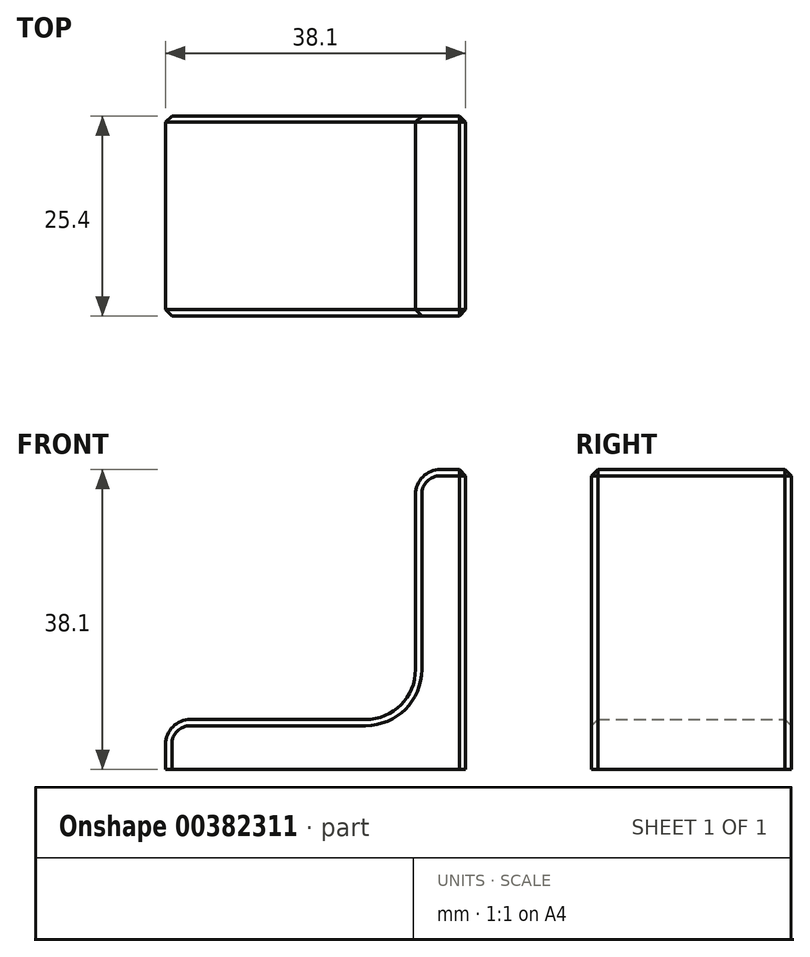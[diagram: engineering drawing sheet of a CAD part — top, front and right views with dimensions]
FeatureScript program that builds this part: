
annotation { "Feature Type Name" : "Feature", "Feature Type Description" : "" }
export const myFeature = defineFeature(function(context is Context, id is Id, definition is map)
    precondition{}
    {
        {
            var Q0;
            Q0=qCreatedBy(makeId("Front.planeOp"),FACE);
            var sketch = newSketch(context, id + "F0", { "sketchPlane" : qUnion([Q0])});
            skLineSegment(sketch, "E0", {"start": v(0, 38.1) * mm, "end": v(0, 0) * mm});
            skLineSegment(sketch, "E1", {"start": v(0, 0) * mm, "end": v(-38.1, 0) * mm});
            skLineSegment(sketch, "E2", {"start": v(-38.1, 0) * mm, "end": v(-38.1, 3.17) * mm});
            skLineSegment(sketch, "E3", {"start": v(0, 38.1) * mm, "end": v(-3.17, 38.1) * mm});
            skLineSegment(sketch, "E4", {"start": v(-6.35, 34.93) * mm, "end": v(-6.35, 12.7) * mm});
            skLineSegment(sketch, "E5", {"start": v(-34.93, 6.35) * mm, "end": v(-12.7, 6.35) * mm});
            skPoint(sketch, "E6.visualSharp", {"position": v(-6.35, 38.1) * mm});
            skArc(sketch, "E6.filletArc", {"start": v(-3.17, 38.1) * mm, "mid": v(-5.42, 37.17) * mm, "end": v(-6.35, 34.93) * mm});
            skPoint(sketch, "E7.visualSharp", {"position": v(-38.1, 6.35) * mm});
            skArc(sketch, "E7.filletArc", {"start": v(-34.93, 6.35) * mm, "mid": v(-37.17, 5.42) * mm, "end": v(-38.1, 3.18) * mm});
            skPoint(sketch, "E8.visualSharp", {"position": v(-6.35, 6.35) * mm});
            skArc(sketch, "E8.filletArc", {"start": v(-12.7, 6.35) * mm, "mid": v(-8.2, 8.2) * mm, "end": v(-6.35, 12.7) * mm});
            skSolve(sketch);
        }
        {
            var Q0;
            Q0=makeQuery(id+"F0.imprint","IMPRINT",FACE,{"disambiguationData":[TD([[makeQuery(id+"F0.imprint","IMPRINT",EDGE,{"derivedFrom":sQuery(id+"F0.wireOp",EDGE,"E0")}),-1.0]])]});
            extrude(context, id + "F1", {"entities" : qUnion([Q0]), "endBound" : BoundingType.SYMMETRIC, "depth" : 25.4 * mm});
        }
        {
            var Q0;
            Q0=makeQuery(id+"F1.opExtrude","CAP_EDGE",EDGE,{"disambiguationData":[OSD([sQuery(id+"F0.wireOp",EDGE,"E5")])],"isStart":false});
            var Q1;
            Q1=makeQuery(id+"F1.opExtrude","CAP_EDGE",EDGE,{"disambiguationData":[OSD([sQuery(id+"F0.wireOp",EDGE,"E8.filletArc")])],"isStart":false});
            var Q2;
            Q2=makeQuery(id+"F1.opExtrude","CAP_EDGE",EDGE,{"disambiguationData":[OSD([sQuery(id+"F0.wireOp",EDGE,"E4")])],"isStart":false});
            var Q3;
            Q3=makeQuery(id+"F1.opExtrude","CAP_EDGE",EDGE,{"disambiguationData":[OSD([sQuery(id+"F0.wireOp",EDGE,"E6.filletArc")])],"isStart":false});
            var Q4;
            Q4=makeQuery(id+"F1.opExtrude","CAP_EDGE",EDGE,{"disambiguationData":[OSD([sQuery(id+"F0.wireOp",EDGE,"E3")])],"isStart":false});
            var Q5;
            Q5=makeQuery(id+"F1.opExtrude","CAP_EDGE",EDGE,{"disambiguationData":[OSD([sQuery(id+"F0.wireOp",EDGE,"E2")])],"isStart":false});
            var Q6;
            Q6=makeQuery(id+"F1.opExtrude","CAP_EDGE",EDGE,{"disambiguationData":[OSD([sQuery(id+"F0.wireOp",EDGE,"E7.filletArc")])],"isStart":false});
            var Q7;
            Q7=makeQuery(id+"F1.opExtrude","CAP_EDGE",EDGE,{"disambiguationData":[OSD([sQuery(id+"F0.wireOp",EDGE,"E3")])],"isStart":true});
            var Q8;
            Q8=makeQuery(id+"F1.opExtrude","CAP_EDGE",EDGE,{"disambiguationData":[OSD([sQuery(id+"F0.wireOp",EDGE,"E6.filletArc")])],"isStart":true});
            var Q9;
            Q9=makeQuery(id+"F1.opExtrude","CAP_EDGE",EDGE,{"disambiguationData":[OSD([sQuery(id+"F0.wireOp",EDGE,"E4")])],"isStart":true});
            var Q10;
            Q10=makeQuery(id+"F1.opExtrude","CAP_EDGE",EDGE,{"disambiguationData":[OSD([sQuery(id+"F0.wireOp",EDGE,"E8.filletArc")])],"isStart":true});
            var Q11;
            Q11=makeQuery(id+"F1.opExtrude","CAP_EDGE",EDGE,{"disambiguationData":[OSD([sQuery(id+"F0.wireOp",EDGE,"E5")])],"isStart":true});
            var Q12;
            Q12=makeQuery(id+"F1.opExtrude","CAP_EDGE",EDGE,{"disambiguationData":[OSD([sQuery(id+"F0.wireOp",EDGE,"E2")])],"isStart":true});
            var Q13;
            Q13=makeQuery(id+"F1.opExtrude","CAP_EDGE",EDGE,{"disambiguationData":[OSD([sQuery(id+"F0.wireOp",EDGE,"E7.filletArc")])],"isStart":true});
            var Q14;
            Q14=makeQuery(id+"F1.opExtrude","CAP_EDGE",EDGE,{"disambiguationData":[OSD([sQuery(id+"F0.wireOp",EDGE,"E0")])],"isStart":true});
            var Q15;
            Q15=makeQuery(id+"F1.opExtrude","CAP_EDGE",EDGE,{"disambiguationData":[OSD([sQuery(id+"F0.wireOp",EDGE,"E0")])],"isStart":false});
            var Q16;
            Q16=makeQuery(id+"F1.opExtrude","SWEPT_EDGE",EDGE,{"disambiguationData":[OSD([sQuery(id+"F0.wireOp",EDGE,"E0"),sQuery(id+"F0.wireOp",EDGE,"E3")])]});
            chamfer(context, id + "F2", {"entities" : qUnion([Q0, Q1, Q2, Q3, Q4, Q5, Q6, Q7, Q8, Q9, Q10, Q11, Q12, Q13, Q14, Q15, Q16]), "width" : 0.8 * mm, "tangentPropagation" : true});
        }
    });
